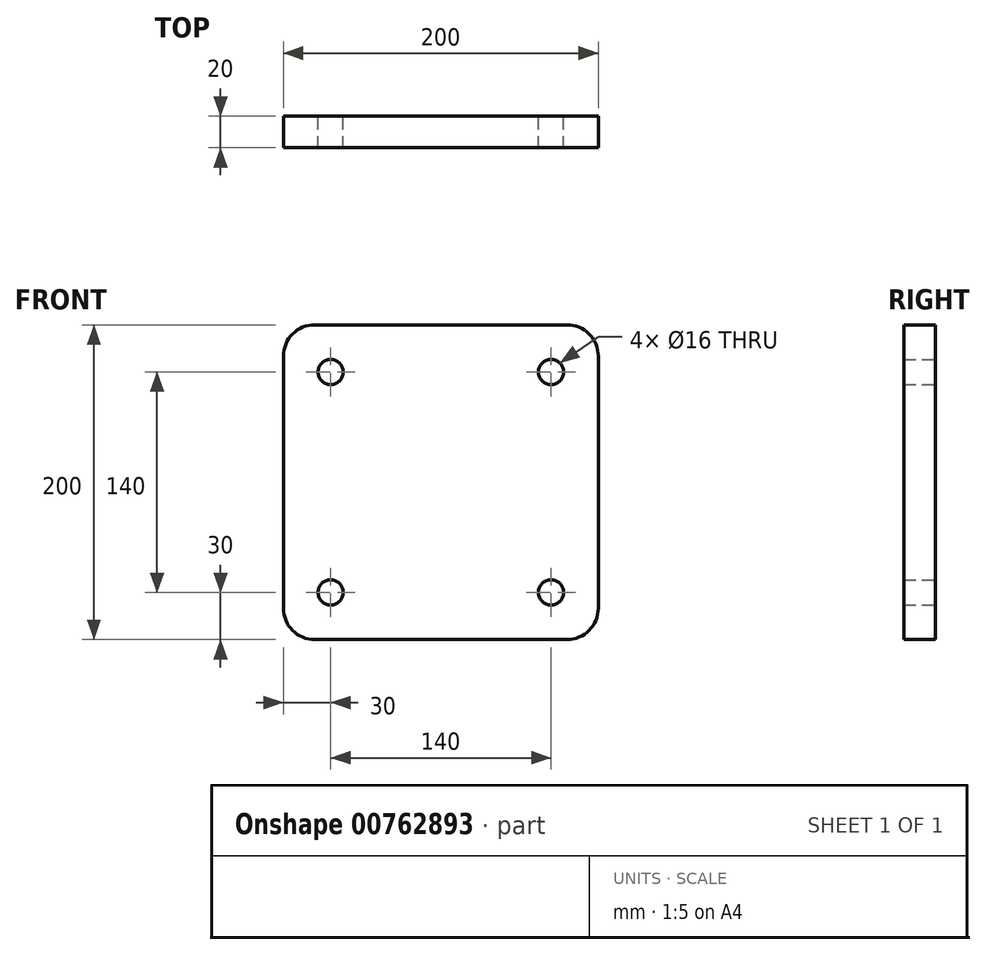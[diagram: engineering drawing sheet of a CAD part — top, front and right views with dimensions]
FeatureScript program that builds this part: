
annotation { "Feature Type Name" : "Feature", "Feature Type Description" : "" }
export const myFeature = defineFeature(function(context is Context, id is Id, definition is map)
    precondition{}
    {
        {
            var Q0;
            Q0=qCreatedBy(makeId("Front.planeOp"),FACE);
            var sketch = newSketch(context, id + "F0", { "sketchPlane" : qUnion([Q0])});
            skLineSegment(sketch, "E0.bottom", {"start": v(80, -100) * mm, "end": v(-80, -100) * mm});
            skLineSegment(sketch, "E0.top", {"start": v(80, 100) * mm, "end": v(-80, 100) * mm});
            skLineSegment(sketch, "E0.left", {"start": v(100, -80) * mm, "end": v(100, 80) * mm});
            skLineSegment(sketch, "E0.right", {"start": v(-100, -80) * mm, "end": v(-100, 80) * mm});
            skPoint(sketch, "E0.middle", {"position": v(0, 0) * mm});
            skPoint(sketch, "E1.visualSharp", {"position": v(-100, 100) * mm});
            skArc(sketch, "E1.filletArc", {"start": v(-80, 100) * mm, "mid": v(-94.14, 94.14) * mm, "end": v(-100, 80) * mm});
            skPoint(sketch, "E2.visualSharp", {"position": v(-100, -100) * mm});
            skArc(sketch, "E2.filletArc", {"start": v(-100, -80) * mm, "mid": v(-94.14, -94.14) * mm, "end": v(-80, -100) * mm});
            skPoint(sketch, "E3.visualSharp", {"position": v(100, -100) * mm});
            skArc(sketch, "E3.filletArc", {"start": v(80, -100) * mm, "mid": v(94.14, -94.14) * mm, "end": v(100, -80) * mm});
            skPoint(sketch, "E4.visualSharp", {"position": v(100, 100) * mm});
            skArc(sketch, "E4.filletArc", {"start": v(100, 80) * mm, "mid": v(94.14, 94.14) * mm, "end": v(80, 100) * mm});
            skCircle(sketch, "E5", {"center": v(-70, 70) * mm, "radius": 8 * mm});
            skCircle(sketch, "E6.MirrorC", {"center": v(70, 70) * mm, "radius": 8 * mm});
            skCircle(sketch, "E7.MirrorC", {"center": v(-70, -70) * mm, "radius": 8 * mm});
            skCircle(sketch, "E8.MirrorC", {"center": v(70, -70) * mm, "radius": 8 * mm});
            skSolve(sketch);
        }
        {
            var Q0;
            Q0=makeQuery(id+"F0.imprint","IMPRINT",FACE,{"disambiguationData":[TD([[makeQuery(id+"F0.imprint","IMPRINT",EDGE,{"derivedFrom":sQuery(id+"F0.wireOp",EDGE,"E0.bottom")}),-1.0]])]});
            extrude(context, id + "F1", {"entities" : qUnion([Q0]), "depth" : 20 * mm, "offsetDistance" : 25 * mm});
        }
    });
